# Revit family: 702-10-103-DN50-600
name_source: partatom
category: Pipe Accessories
units: mm (PartAtom-declared; Revit-internal decimal feet)

## family parameters
Always vertical = Yes
Cut with Voids When Loaded = No
Part Type = Valve - Breaks Into
Round Connector Dimension = Use Diameter
Shared = No
Work Plane-Based = No

## types (14) — shared parameters
DN050_PN10 = 702-0050-10-0000141
DN065_PN10 = 702-0065-10-0000141
DN080_PN10 = 702-0080-10-0000143
DN100_PN10 = 702-0100-10-0000152
DN125_PN10 = 702-0125-10-0000154
DN150_PN10 = 702-0150-10-0000155
DN200_PN10 = 702-0200-10-0000031
DN250_PN10 = 702-0250-10-0000031
DN300_PN10 = 702-0300-10-0000028
DN350_PN10 = 702-0350-10-0000031
DN400_PN10 = 702-0400-10-0000020
DN450_PN10 = 702-0450-10-0000025
DN500_PN10 = 702-0500-10-0000017
DN600_PN10 = 702-0600-10-0000017
Description_ = AVK KNIFE GATE VALVE
Search_table = 702-10-103-DN50-600
URL product pages = https://www.avkvalves.com 7020100100000152

## per-type parameters (varying)
| type | B2_Ref | Body_width | Body_width_2 | Bonnet_height | Bonnet_height_2 | D | Fillet_Radius | Flange_Thickness | H | H3 | HW_Dia | HW_Rib | H_Ref | Hc_Ref | ID | L | L2 | Name_Ref | Neck_Rod | Nominal Diameter (DN) | W | W2 | W3 |
| DN050_PN10 | 79 mm | 87 mm | 70 mm | 265 mm | 146 mm | 78 mm  [stored 0.255906 ft] | 5 mm  [stored 0.0164042 ft] | 5 mm  [stored 0.0164042 ft] | 292 mm | 357 mm | 20 mm  [stored 0.0656168 ft] | 145 mm | 114 mm | 282 mm | 25 mm  [stored 0.082021 ft] | 43 mm  [stored 0.141076 ft] | 47 mm | 170 mm | 10 mm  [stored 0.0328084 ft] | 50 mm  [stored 0.164042 ft] | 131 mm | 66 mm  [stored 0.216535 ft] | 55 mm |
| DN065_PN10 | 86 mm | 95 mm | 76 mm | 288 mm | 159 mm | 78 mm  [stored 0.255906 ft] | 5 mm  [stored 0.0164042 ft] | 5 mm  [stored 0.0164042 ft] | 317 mm | 389 mm | 20 mm  [stored 0.0656168 ft] | 145 mm | 124 mm | 307 mm | 33 mm | 46 mm  [stored 0.150919 ft] | 51 mm | 186 mm | 10 mm  [stored 0.0328084 ft] | 65 mm  [stored 0.213255 ft] | 143 mm | 72 mm | 60 mm  [stored 0.19685 ft] |
| DN080_PN10 | 110 mm | 123 mm | 98 mm | 328 mm | 181 mm | 103 mm | 5 mm  [stored 0.0164042 ft] | 5 mm  [stored 0.0164042 ft] | 361 mm | 453 mm | 20 mm  [stored 0.0656168 ft] | 195 mm | 159 mm | 351 mm | 40 mm  [stored 0.131234 ft] | 46 mm  [stored 0.150919 ft] | 51 mm | 239 mm | 10 mm  [stored 0.0328084 ft] | 80 mm  [stored 0.262467 ft] | 184 mm | 92 mm  [stored 0.301837 ft] | 77 mm |
| DN100_PN10 | 121 mm | 135 mm | 108 mm | 360 mm | 198 mm | 103 mm | 10 mm  [stored 0.0328084 ft] | 5 mm  [stored 0.0164042 ft] | 396 mm | 497 mm | 20 mm  [stored 0.0656168 ft] | 195 mm | 175 mm | 386 mm | 50 mm  [stored 0.164042 ft] | 52 mm | 57 mm | 263 mm | 10 mm  [stored 0.0328084 ft] | 100 mm  [stored 0.328084 ft] | 202 mm | 101 mm | 84 mm |
| DN125_PN10 | 138 mm | 153 mm | 123 mm | 393 mm | 216 mm | 103 mm | 10 mm  [stored 0.0328084 ft] | 5 mm  [stored 0.0164042 ft] | 432 mm | 547 mm | 20 mm  [stored 0.0656168 ft] | 195 mm | 199 mm | 422 mm | 63 mm | 56 mm  [stored 0.183727 ft] | 62 mm | 299 mm | 10 mm  [stored 0.0328084 ft] | 125 mm | 230 mm | 115 mm | 96 mm |
| DN150_PN10 | 162 mm | 180 mm | 144 mm | 475 mm | 262 mm | 140 mm | 10 mm  [stored 0.0328084 ft] | 5 mm  [stored 0.0164042 ft] | 523 mm | 658 mm | 20 mm  [stored 0.0656168 ft] | 270 mm | 234 mm | 513 mm | 75 mm | 56 mm  [stored 0.183727 ft] | 62 mm | 351 mm | 10 mm  [stored 0.0328084 ft] | 150 mm | 270 mm | 135 mm | 113 mm |
| DN200_PN10 | 199 mm | 221 mm | 177 mm | 566 mm | 312 mm | 130 mm | 15 mm  [stored 0.0492126 ft] | 10 mm  [stored 0.0328084 ft] | 623 mm | 788 mm | 40 mm  [stored 0.131234 ft] | 240 mm | 287 mm | 603 mm | 100 mm  [stored 0.328084 ft] | 60 mm  [stored 0.19685 ft] | 66 mm  [stored 0.216535 ft] | 430 mm | 20 mm  [stored 0.0656168 ft] | 200 mm | 331 mm | 166 mm | 138 mm |
| DN250_PN10 | 238 mm | 265 mm | 212 mm | 663 mm | 365 mm | 130 mm | 15 mm  [stored 0.0492126 ft] | 10 mm  [stored 0.0328084 ft] | 729 mm | 927 mm | 40 mm  [stored 0.131234 ft] | 240 mm | 344 mm | 709 mm | 125 mm | 68 mm  [stored 0.223097 ft] | 75 mm | 516 mm | 20 mm  [stored 0.0656168 ft] | 250 mm | 397 mm | 199 mm | 165 mm |
| DN300_PN10 | 271 mm | 301 mm | 241 mm | 780 mm | 429 mm | 170 mm | 15 mm  [stored 0.0492126 ft] | 15 mm  [stored 0.0492126 ft] | 858 mm | 1084 mm | 60 mm  [stored 0.19685 ft] | 310 mm | 392 mm | 828 mm | 150 mm | 78 mm  [stored 0.255906 ft] | 86 mm | 588 mm | 25 mm  [stored 0.082021 ft] | 300 mm | 452 mm | 226 mm | 188 mm |
| DN350_PN10 | 311 mm | 345 mm | 276 mm | 865 mm | 476 mm | 170 mm | 20 mm  [stored 0.0656168 ft] | 15 mm  [stored 0.0492126 ft] | 951 mm | 1210 mm | 60 mm  [stored 0.19685 ft] | 310 mm | 449 mm | 921 mm | 175 mm | 78 mm  [stored 0.255906 ft] | 86 mm | 673 mm | 25 mm  [stored 0.082021 ft] | 350 mm | 518 mm | 259 mm | 216 mm |
| DN400_PN10 | 346 mm | 384 mm | 307 mm | 963 mm | 530 mm | 160 mm | 20 mm  [stored 0.0656168 ft] | 20 mm  [stored 0.0656168 ft] | 1059 mm | 1347 mm | 80 mm  [stored 0.262467 ft] | 280 mm | 499 mm | 1019 mm | 200 mm | 90 mm  [stored 0.295276 ft] | 99 mm  [stored 0.324803 ft] | 749 mm | 20 mm  [stored 0.0656168 ft] | 400 mm | 576 mm | 288 mm | 240 mm |
| DN450_PN10 | 328 mm | 364 mm | 291 mm | 1096 mm | 603 mm | 210 mm | 20 mm  [stored 0.0656168 ft] | 20 mm  [stored 0.0656168 ft] | 1206 mm | 1519 mm | 80 mm  [stored 0.262467 ft] | 380 mm | 473 mm | 1166 mm | 225 mm | 90 mm  [stored 0.295276 ft] | 99 mm  [stored 0.324803 ft] | 710 mm | 20 mm  [stored 0.0656168 ft] | 450 mm | 546 mm | 273 mm | 228 mm |
| DN500_PN10 | 419 mm | 465 mm | 372 mm | 1189 mm | 654 mm | 210 mm | 25 mm  [stored 0.082021 ft] | 20 mm  [stored 0.0656168 ft] | 1308 mm | 1657 mm | 80 mm  [stored 0.262467 ft] | 380 mm | 605 mm | 1268 mm | 250 mm | 95 mm | 105 mm | 907 mm | 20 mm  [stored 0.0656168 ft] | 500 mm | 698 mm | 349 mm | 291 mm |
| DN600_PN10 | 490 mm | 545 mm | 436 mm | 1361 mm | 749 mm | 210 mm | 25 mm  [stored 0.082021 ft] | 20 mm  [stored 0.0656168 ft] | 1497 mm | 1905 mm | 80 mm  [stored 0.262467 ft] | 380 mm | 708 mm | 1457 mm | 300 mm | 105 mm | 116 mm | 1062 mm | 20 mm  [stored 0.0656168 ft] | 600 mm | 817 mm | 409 mm | 340 mm |

note: [stored X ft] marks values corroborated as IEEE doubles in the binary element streams (Revit-internal decimal feet)

## geometry (parser evidence)
native form markers: Sweep x6
no freeform markers — native parametric forms only
